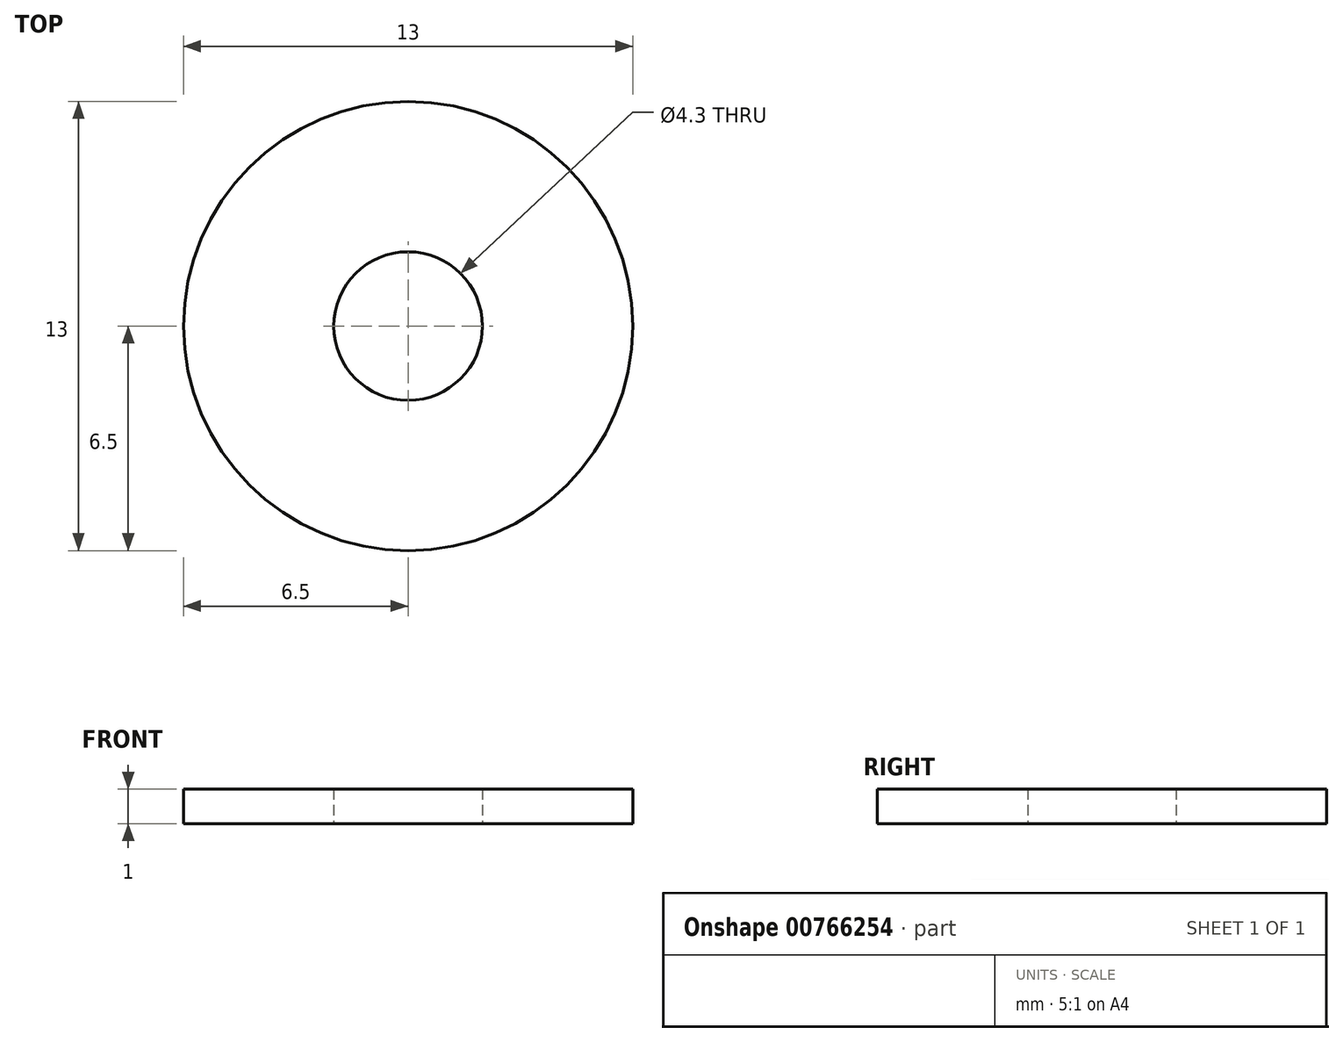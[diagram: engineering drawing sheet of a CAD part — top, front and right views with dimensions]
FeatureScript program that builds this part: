
annotation { "Feature Type Name" : "Feature", "Feature Type Description" : "" }
export const myFeature = defineFeature(function(context is Context, id is Id, definition is map)
    precondition{}
    {
        {
            var Q0;
            Q0=qCreatedBy(makeId("Top.planeOp"),FACE);
            var sketch = newSketch(context, id + "F0", { "sketchPlane" : qUnion([Q0])});
            skCircle(sketch, "E0", {"center": v(0, 0) * mm, "radius": 2.15 * mm});
            skCircle(sketch, "E1", {"center": v(0, 0) * mm, "radius": 6.5 * mm});
            skSolve(sketch);
        }
        {
            var Q0;
            Q0 = qSketchRegion(id + "F0", true);
            extrude(context, id + "F1", {"entities" : qUnion([Q0]), "depth" : 1 * mm, "offsetDistance" : 25 * mm});
        }
    });
